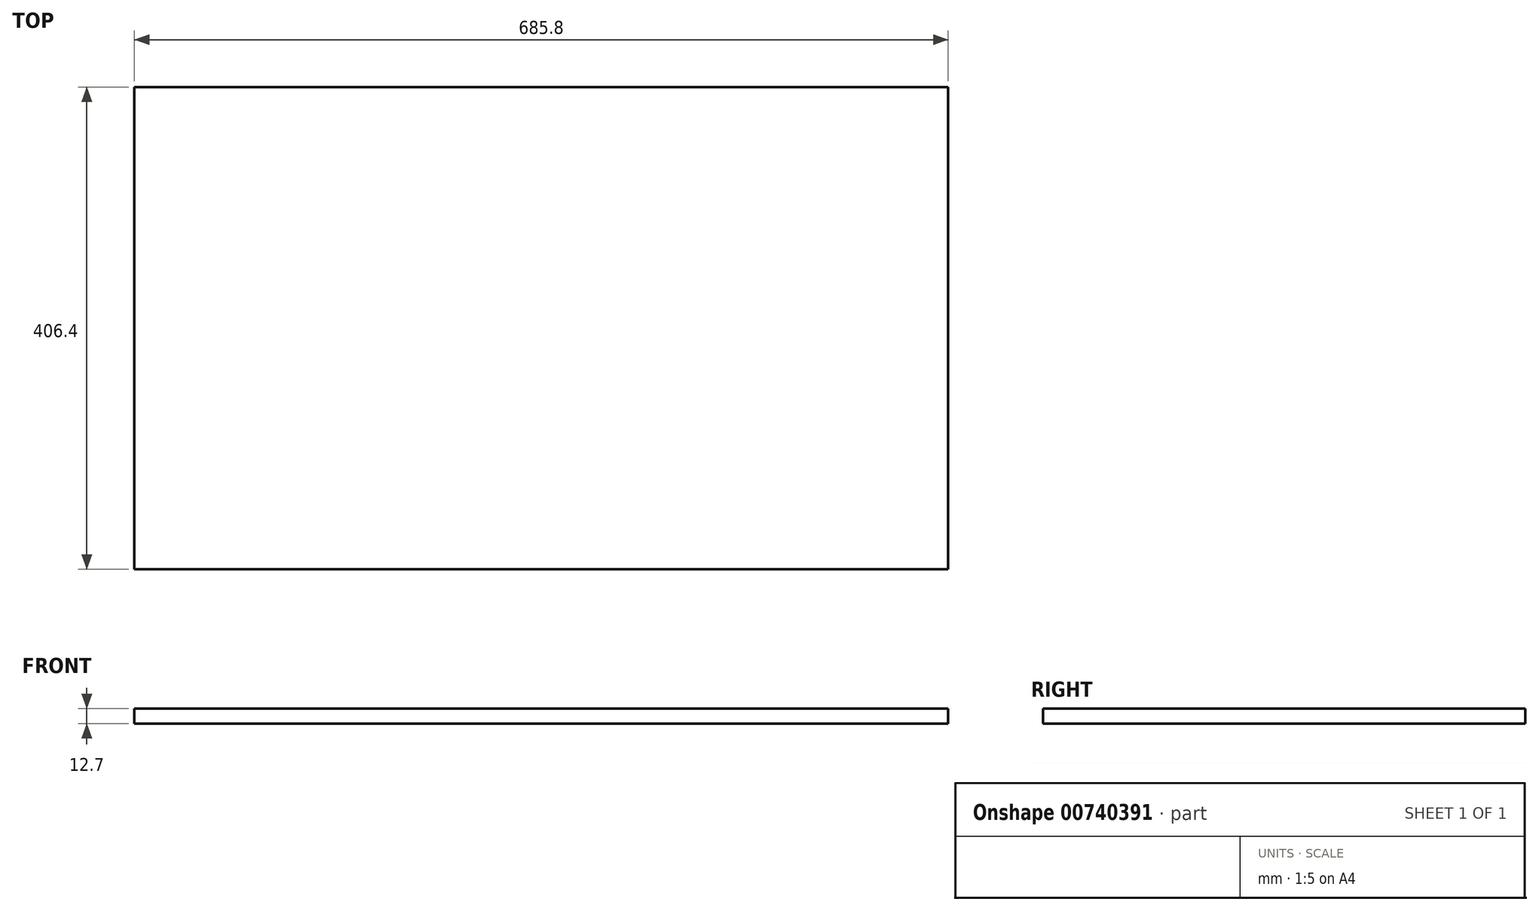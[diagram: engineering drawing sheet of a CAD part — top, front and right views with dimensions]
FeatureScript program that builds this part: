
annotation { "Feature Type Name" : "Feature", "Feature Type Description" : "" }
export const myFeature = defineFeature(function(context is Context, id is Id, definition is map)
    precondition{}
    {
        {
            var Q0;
            Q0=qCreatedBy(makeId("Top.planeOp"),FACE);
            var sketch = newSketch(context, id + "F0", { "sketchPlane" : qUnion([Q0])});
            skLineSegment(sketch, "E0.bottom", {"start": v(342.9, 203.2) * mm, "end": v(-342.9, 203.2) * mm});
            skLineSegment(sketch, "E0.top", {"start": v(342.9, -203.2) * mm, "end": v(-342.9, -203.2) * mm});
            skLineSegment(sketch, "E0.left", {"start": v(342.9, 203.2) * mm, "end": v(342.9, -203.2) * mm});
            skLineSegment(sketch, "E0.right", {"start": v(-342.9, 203.2) * mm, "end": v(-342.9, -203.2) * mm});
            skPoint(sketch, "E0.middle", {"position": v(0, 0) * mm});
            skSolve(sketch);
        }
        {
            var Q0;
            Q0=makeQuery(id+"F0.imprint","IMPRINT",FACE,{"disambiguationData":[TD([[makeQuery(id+"F0.imprint","IMPRINT",EDGE,{"derivedFrom":sQuery(id+"F0.wireOp",EDGE,"E0.bottom")}),1.0]])]});
            extrude(context, id + "F1", {"entities" : qUnion([Q0]), "depth" : 12.7 * mm, "offsetDistance" : 25.4 * mm});
        }
    });
